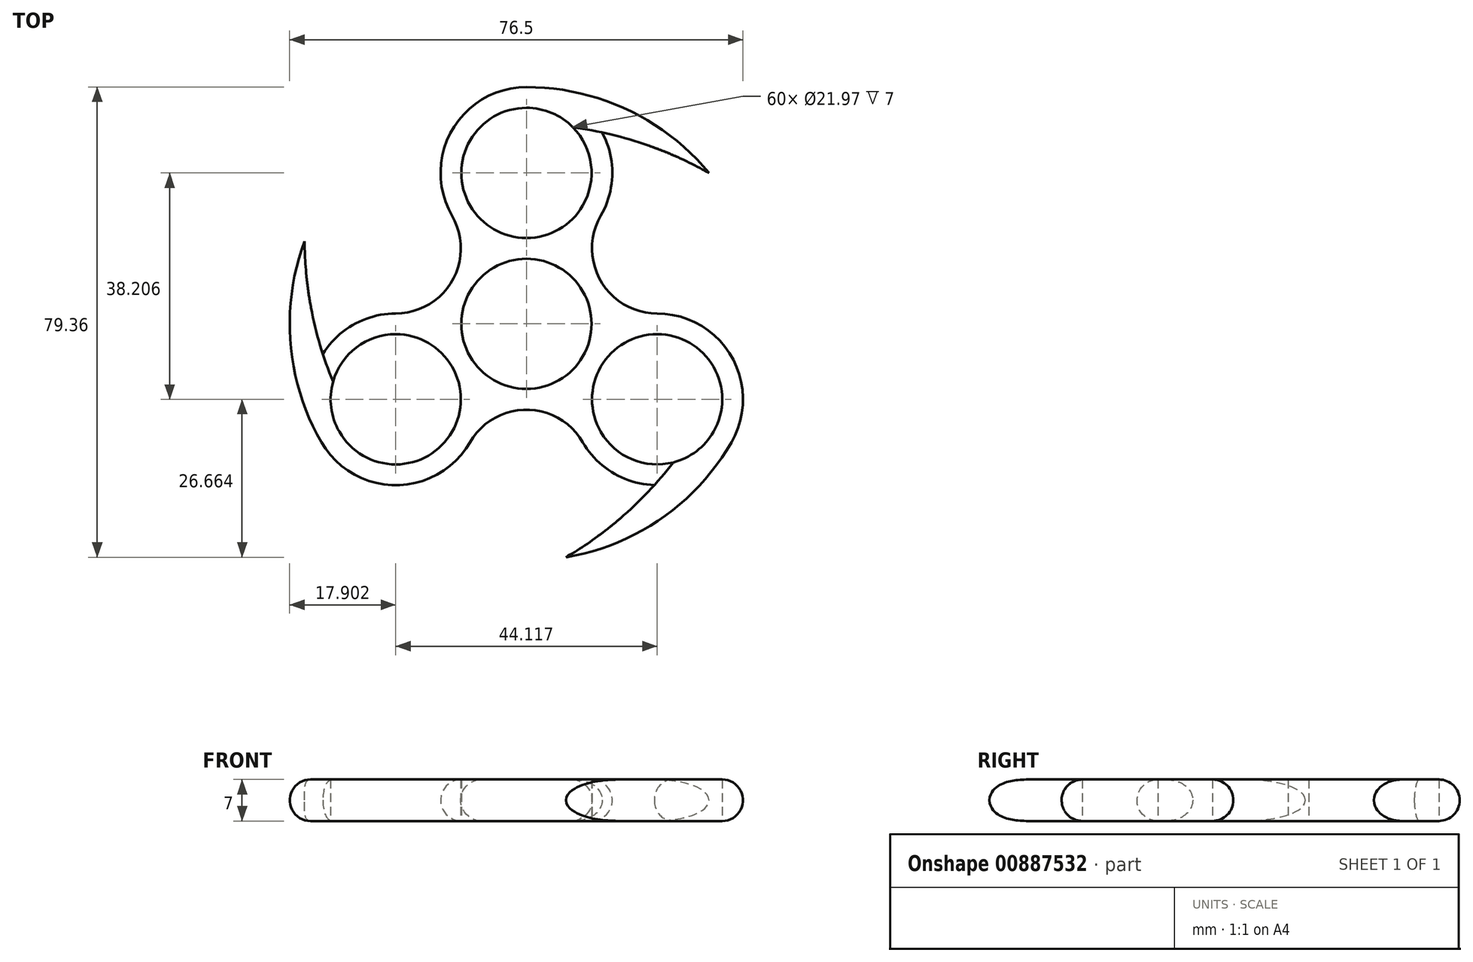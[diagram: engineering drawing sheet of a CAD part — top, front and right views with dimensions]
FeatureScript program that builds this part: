
annotation { "Feature Type Name" : "Feature", "Feature Type Description" : "" }
export const myFeature = defineFeature(function(context is Context, id is Id, definition is map)
    precondition{}
    {
        {
            var Q0;
            Q0=qCreatedBy(makeId("Top.planeOp"),FACE);
            var sketch = newSketch(context, id + "F0", { "sketchPlane" : qUnion([Q0])});
            skCircle(sketch, "E0", {"center": v(0, 0) * mm, "radius": 10.99 * mm});
            skCircle(sketch, "E1", {"center": v(0, 0) * mm, "radius": 25.47 * mm, "construction": true});
            skCircle(sketch, "E2", {"center": v(0, 25.47) * mm, "radius": 10.99 * mm});
            skCircle(sketch, "E3", {"center": v(-22.06, -12.74) * mm, "radius": 10.99 * mm});
            skCircle(sketch, "E4", {"center": v(22.06, -12.74) * mm, "radius": 10.99 * mm});
            skLineSegment(sketch, "E5", {"start": v(-22.06, -12.74) * mm, "end": v(22.06, -12.74) * mm, "construction": true});
            skLineSegment(sketch, "E6", {"start": v(0, 25.47) * mm, "end": v(-22.06, -12.74) * mm, "construction": true});
            skLineSegment(sketch, "E7", {"start": v(22.06, -12.74) * mm, "end": v(0, 25.47) * mm, "construction": true});
            skLineSegment(sketch, "E8.bottom", {"start": v(-57.15, 57.15) * mm, "end": v(57.15, 57.15) * mm, "construction": true});
            skLineSegment(sketch, "E8.top", {"start": v(-57.15, -57.15) * mm, "end": v(57.15, -57.15) * mm, "construction": true});
            skLineSegment(sketch, "E8.left", {"start": v(-57.15, 57.15) * mm, "end": v(-57.15, -57.15) * mm, "construction": true});
            skLineSegment(sketch, "E8.right", {"start": v(57.15, 57.15) * mm, "end": v(57.15, -57.15) * mm, "construction": true});
            skPoint(sketch, "E9", {"position": v(-57.15, 0) * mm});
            skPoint(sketch, "E10", {"position": v(0, 57.15) * mm});
            skSolve(sketch);
        }
        {
            var Q0;
            Q0=qCreatedBy(makeId("Top.planeOp"),FACE);
            var sketch = newSketch(context, id + "F1", { "sketchPlane" : qUnion([Q0])});
            skCircle(sketch, "E11", {"center": v(0, 0) * mm, "radius": 10.99 * mm});
            skCircle(sketch, "E12", {"center": v(-22.06, -12.74) * mm, "radius": 10.99 * mm});
            skCircle(sketch, "E13", {"center": v(0, 25.47) * mm, "radius": 10.99 * mm});
            skCircle(sketch, "E14", {"center": v(22.06, -12.74) * mm, "radius": 10.99 * mm});
            skLineSegment(sketch, "E15.bottom", {"start": v(-57.15, 57.15) * mm, "end": v(57.15, 57.15) * mm, "construction": true});
            skLineSegment(sketch, "E15.top", {"start": v(-57.15, -57.15) * mm, "end": v(57.15, -57.15) * mm, "construction": true});
            skLineSegment(sketch, "E15.left", {"start": v(-57.15, 57.15) * mm, "end": v(-57.15, -57.15) * mm, "construction": true});
            skLineSegment(sketch, "E15.right", {"start": v(57.15, 57.15) * mm, "end": v(57.15, -57.15) * mm, "construction": true});
            skPoint(sketch, "E16", {"position": v(-57.15, 0) * mm});
            skPoint(sketch, "E17", {"position": v(0, 57.15) * mm});
            skArc(sketch, "E18", {"start": v(-22.06, 1.75) * mm, "mid": v(-29.1, -0.07) * mm, "end": v(-34.36, -5.09) * mm});
            skArc(sketch, "E19", {"start": v(12.54, 18.23) * mm, "mid": v(14.48, 25.23) * mm, "end": v(12.77, 32.3) * mm});
            skArc(sketch, "E20", {"start": v(9.51, -19.98) * mm, "mid": v(14.61, -25.16) * mm, "end": v(21.59, -27.21) * mm});
            skArc(sketch, "E21", {"start": v(-22.06, 1.75) * mm, "mid": v(-12.54, 7.24) * mm, "end": v(-12.54, 18.23) * mm});
            skArc(sketch, "E22", {"start": v(12.54, 18.23) * mm, "mid": v(12.54, 7.24) * mm, "end": v(22.06, 1.75) * mm});
            skArc(sketch, "E23", {"start": v(9.51, -19.98) * mm, "mid": v(0, -14.49) * mm, "end": v(-9.51, -19.98) * mm});
            skCircle(sketch, "E24", {"center": v(0, 0) * mm, "radius": 14.49 * mm, "construction": true});
            skArc(sketch, "E25", {"start": v(30.79, 25.47) * mm, "mid": v(17.01, 36.15) * mm, "end": v(0, 39.96) * mm});
            skArc(sketch, "E26", {"start": v(30.79, 25.47) * mm, "mid": v(22.04, 29.57) * mm, "end": v(12.77, 32.3) * mm});
            skArc(sketch, "E27.1.0", {"start": v(-37.45, 13.93) * mm, "mid": v(-39.82, -3.34) * mm, "end": v(-34.6, -19.98) * mm});
            skArc(sketch, "E27.1.1", {"start": v(-37.45, 13.93) * mm, "mid": v(-36.63, 4.3) * mm, "end": v(-34.36, -5.09) * mm});
            skArc(sketch, "E27.2.0", {"start": v(6.66, -39.4) * mm, "mid": v(22.8, -32.81) * mm, "end": v(34.6, -19.98) * mm});
            skArc(sketch, "E27.2.1", {"start": v(6.66, -39.4) * mm, "mid": v(14.59, -33.88) * mm, "end": v(21.59, -27.21) * mm});
            skArc(sketch, "E28.trimOffspring", {"start": v(0, 39.96) * mm, "mid": v(-12.54, 32.71) * mm, "end": v(-12.54, 18.23) * mm});
            skArc(sketch, "E29.trimOffspring", {"start": v(34.6, -19.98) * mm, "mid": v(34.6, -5.5) * mm, "end": v(22.06, 1.75) * mm});
            skArc(sketch, "E30.trimOffspring", {"start": v(-34.6, -19.98) * mm, "mid": v(-22.06, -27.22) * mm, "end": v(-9.51, -19.98) * mm});
            skSolve(sketch);
        }
        {
            var Q0;
            Q0=makeQuery(id+"F1.imprint","IMPRINT",FACE,{"disambiguationData":[TD([[makeQuery(id+"F1.imprint","IMPRINT",EDGE,{"derivedFrom":sQuery(id+"F1.wireOp",EDGE,"E11")}),-1.0]])]});
            extrude(context, id + "F2", {"entities" : qUnion([Q0]), "depth" : 7 * mm, "offsetDistance" : 25.4 * mm});
        }
        {
            var Q0;
            Q0=makeQuery(id+"F2.opExtrude","CAP_EDGE",EDGE,{"disambiguationData":[OSD([sQuery(id+"F1.wireOp",EDGE,"E22")])],"isStart":false});
            var Q1;
            Q1=makeQuery(id+"F2.opExtrude","CAP_EDGE",EDGE,{"disambiguationData":[OSD([sQuery(id+"F1.wireOp",EDGE,"E23")])],"isStart":false});
            var Q2;
            Q2=makeQuery(id+"F2.opExtrude","CAP_EDGE",EDGE,{"disambiguationData":[OSD([sQuery(id+"F1.wireOp",EDGE,"E21")])],"isStart":false});
            var Q3;
            Q3=makeQuery(id+"F2.opExtrude","CAP_EDGE",EDGE,{"disambiguationData":[OSD([sQuery(id+"F1.wireOp",EDGE,"E29.trimOffspring")])],"isStart":true});
            var Q4;
            Q4=makeQuery(id+"F2.opExtrude","CAP_EDGE",EDGE,{"disambiguationData":[OSD([sQuery(id+"F1.wireOp",EDGE,"E30.trimOffspring")])],"isStart":true});
            var Q5;
            Q5=makeQuery(id+"F2.opExtrude","CAP_EDGE",EDGE,{"disambiguationData":[OSD([sQuery(id+"F1.wireOp",EDGE,"E21")])],"isStart":true});
            fillet(context, id + "F3", {"entities" : qUnion([Q0, Q1, Q2, Q3, Q4, Q5]), "radius" : 3.5 * mm, "tangentPropagation" : true, "allowEdgeOverflow" : false});
        }
    });
